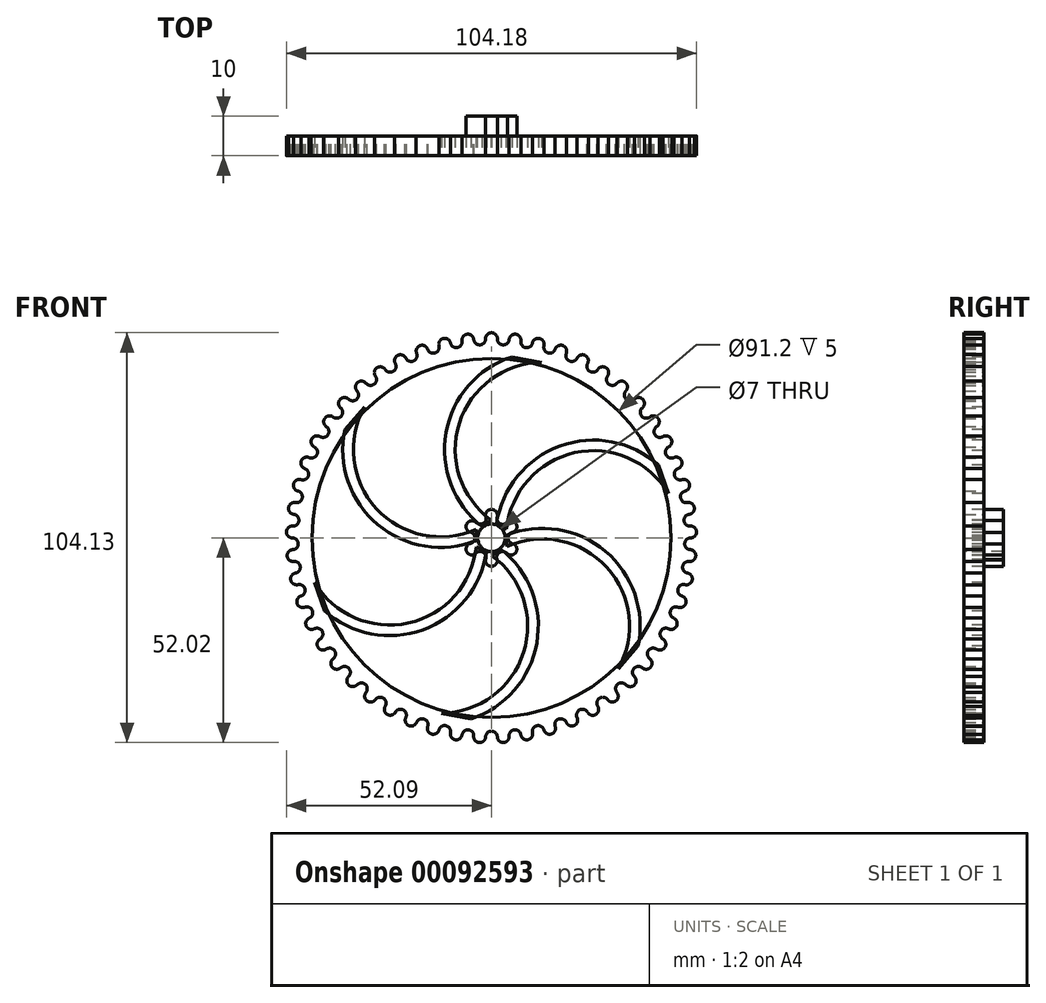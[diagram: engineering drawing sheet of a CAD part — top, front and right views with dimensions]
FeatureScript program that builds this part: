
annotation { "Feature Type Name" : "Feature", "Feature Type Description" : "" }
export const myFeature = defineFeature(function(context is Context, id is Id, definition is map)
    precondition{}
    {
        {
            var Q0;
            Q0=qCreatedBy(makeId("Front.planeOp"),FACE);
            var sketch = newSketch(context, id + "F0", { "sketchPlane" : qUnion([Q0])});
            skLineSegment(sketch, "E0", {"start": v(0, 0) * mm, "end": v(0, 50.61) * mm});
            skArc(sketch, "E1", {"start": v(1.5, 50.57) * mm, "mid": v(0.01, 52.11) * mm, "end": v(-1.5, 50.59) * mm});
            skArc(sketch, "E2", {"start": v(1.5, 50.57) * mm, "mid": v(2.92, 49.02) * mm, "end": v(4.5, 50.41) * mm});
            skLineSegment(sketch, "E3", {"start": v(4.5, 50.41) * mm, "end": v(4.47, 50.43) * mm});
            skArc(sketch, "E4.1.0", {"start": v(-4.5, 50.39) * mm, "mid": v(-6.15, 51.75) * mm, "end": v(-7.47, 50.06) * mm});
            skArc(sketch, "E4.1.1", {"start": v(-4.5, 50.39) * mm, "mid": v(-2.9, 49.03) * mm, "end": v(-1.5, 50.59) * mm});
            skLineSegment(sketch, "E4.1.2", {"start": v(-1.5, 50.59) * mm, "end": v(-1.52, 50.6) * mm});
            skArc(sketch, "E4.2.0", {"start": v(-10.42, 49.5) * mm, "mid": v(-12.23, 50.66) * mm, "end": v(-13.34, 48.82) * mm});
            skArc(sketch, "E4.2.1", {"start": v(-10.42, 49.5) * mm, "mid": v(-8.68, 48.34) * mm, "end": v(-7.47, 50.06) * mm});
            skLineSegment(sketch, "E4.2.2", {"start": v(-7.47, 50.06) * mm, "end": v(-7.5, 50.07) * mm});
            skArc(sketch, "E4.3.0", {"start": v(-16.2, 47.92) * mm, "mid": v(-18.13, 48.85) * mm, "end": v(-19.02, 46.9) * mm});
            skArc(sketch, "E4.3.1", {"start": v(-16.2, 47.92) * mm, "mid": v(-14.33, 46.97) * mm, "end": v(-13.34, 48.82) * mm});
            skLineSegment(sketch, "E4.3.2", {"start": v(-13.34, 48.82) * mm, "end": v(-13.37, 48.84) * mm});
            skArc(sketch, "E4.4.0", {"start": v(-21.76, 45.67) * mm, "mid": v(-23.79, 46.37) * mm, "end": v(-24.43, 44.32) * mm});
            skArc(sketch, "E4.4.1", {"start": v(-21.76, 45.67) * mm, "mid": v(-19.79, 44.95) * mm, "end": v(-19.02, 46.9) * mm});
            skLineSegment(sketch, "E4.4.2", {"start": v(-19.02, 46.9) * mm, "end": v(-19.05, 46.91) * mm});
            skArc(sketch, "E4.5.0", {"start": v(-27, 42.78) * mm, "mid": v(-29.1, 43.23) * mm, "end": v(-29.5, 41.12) * mm});
            skArc(sketch, "E4.5.1", {"start": v(-27, 42.78) * mm, "mid": v(-24.96, 42.3) * mm, "end": v(-24.43, 44.32) * mm});
            skLineSegment(sketch, "E4.5.2", {"start": v(-24.43, 44.32) * mm, "end": v(-24.46, 44.33) * mm});
            skArc(sketch, "E4.6.0", {"start": v(-31.88, 39.28) * mm, "mid": v(-34.01, 39.48) * mm, "end": v(-34.16, 37.34) * mm});
            skArc(sketch, "E4.6.1", {"start": v(-31.88, 39.28) * mm, "mid": v(-29.8, 39.04) * mm, "end": v(-29.5, 41.12) * mm});
            skLineSegment(sketch, "E4.6.2", {"start": v(-29.5, 41.12) * mm, "end": v(-29.54, 41.13) * mm});
            skArc(sketch, "E4.7.0", {"start": v(-36.3, 35.24) * mm, "mid": v(-38.44, 35.18) * mm, "end": v(-38.34, 33.04) * mm});
            skArc(sketch, "E4.7.1", {"start": v(-36.3, 35.24) * mm, "mid": v(-34.2, 35.25) * mm, "end": v(-34.16, 37.34) * mm});
            skLineSegment(sketch, "E4.7.2", {"start": v(-34.16, 37.34) * mm, "end": v(-34.2, 37.34) * mm});
            skArc(sketch, "E4.8.0", {"start": v(-40.21, 30.7) * mm, "mid": v(-42.33, 30.39) * mm, "end": v(-41.98, 28.27) * mm});
            skArc(sketch, "E4.8.1", {"start": v(-40.21, 30.7) * mm, "mid": v(-38.13, 30.95) * mm, "end": v(-38.34, 33.04) * mm});
            skLineSegment(sketch, "E4.8.2", {"start": v(-38.34, 33.04) * mm, "end": v(-38.37, 33.04) * mm});
            skArc(sketch, "E4.9.0", {"start": v(-43.56, 25.73) * mm, "mid": v(-45.63, 25.17) * mm, "end": v(-45.03, 23.11) * mm});
            skArc(sketch, "E4.9.1", {"start": v(-43.56, 25.73) * mm, "mid": v(-41.52, 26.23) * mm, "end": v(-41.98, 28.27) * mm});
            skLineSegment(sketch, "E4.9.2", {"start": v(-41.98, 28.27) * mm, "end": v(-42, 28.27) * mm});
            skArc(sketch, "E4.10.0", {"start": v(-46.3, 20.4) * mm, "mid": v(-48.29, 19.6) * mm, "end": v(-47.44, 17.62) * mm});
            skArc(sketch, "E4.10.1", {"start": v(-46.3, 20.4) * mm, "mid": v(-44.33, 21.13) * mm, "end": v(-45.03, 23.11) * mm});
            skLineSegment(sketch, "E4.10.2", {"start": v(-45.03, 23.11) * mm, "end": v(-45.06, 23.1) * mm});
            skArc(sketch, "E4.11.0", {"start": v(-48.38, 14.78) * mm, "mid": v(-50.27, 13.75) * mm, "end": v(-49.2, 11.89) * mm});
            skArc(sketch, "E4.11.1", {"start": v(-48.38, 14.78) * mm, "mid": v(-46.52, 15.74) * mm, "end": v(-47.44, 17.62) * mm});
            skLineSegment(sketch, "E4.11.2", {"start": v(-47.44, 17.62) * mm, "end": v(-47.47, 17.6) * mm});
            skArc(sketch, "E4.12.0", {"start": v(-49.8, 8.95) * mm, "mid": v(-51.54, 7.7) * mm, "end": v(-50.26, 5.99) * mm});
            skArc(sketch, "E4.12.1", {"start": v(-49.8, 8.95) * mm, "mid": v(-48.06, 10.13) * mm, "end": v(-49.2, 11.89) * mm});
            skLineSegment(sketch, "E4.12.2", {"start": v(-49.2, 11.89) * mm, "end": v(-49.22, 11.87) * mm});
            skArc(sketch, "E4.13.0", {"start": v(-50.5, 3) * mm, "mid": v(-52.09, 1.56) * mm, "end": v(-50.61, 0) * mm});
            skArc(sketch, "E4.13.1", {"start": v(-50.5, 3) * mm, "mid": v(-48.92, 4.37) * mm, "end": v(-50.26, 5.99) * mm});
            skLineSegment(sketch, "E4.13.2", {"start": v(-50.26, 5.99) * mm, "end": v(-50.28, 5.97) * mm});
            skArc(sketch, "E4.14.0", {"start": v(-50.5, -3) * mm, "mid": v(-51.9, -4.62) * mm, "end": v(-50.26, -5.99) * mm});
            skArc(sketch, "E4.14.1", {"start": v(-50.5, -3) * mm, "mid": v(-49.1, -1.44) * mm, "end": v(-50.61, 0) * mm});
            skLineSegment(sketch, "E4.14.2", {"start": v(-50.61, 0) * mm, "end": v(-50.63, -0.02) * mm});
            skArc(sketch, "E4.15.0", {"start": v(-49.8, -8.95) * mm, "mid": v(-51, -10.72) * mm, "end": v(-49.2, -11.89) * mm});
            skArc(sketch, "E4.15.1", {"start": v(-49.8, -8.95) * mm, "mid": v(-48.57, -7.24) * mm, "end": v(-50.26, -5.99) * mm});
            skLineSegment(sketch, "E4.15.2", {"start": v(-50.26, -5.99) * mm, "end": v(-50.27, -6.01) * mm});
            skArc(sketch, "E4.16.0", {"start": v(-48.38, -14.77) * mm, "mid": v(-49.37, -16.68) * mm, "end": v(-47.44, -17.62) * mm});
            skArc(sketch, "E4.16.1", {"start": v(-48.38, -14.77) * mm, "mid": v(-47.38, -12.93) * mm, "end": v(-49.2, -11.89) * mm});
            skLineSegment(sketch, "E4.16.2", {"start": v(-49.2, -11.89) * mm, "end": v(-49.21, -11.91) * mm});
            skArc(sketch, "E4.17.0", {"start": v(-46.3, -20.4) * mm, "mid": v(-47.05, -22.4) * mm, "end": v(-45.03, -23.11) * mm});
            skArc(sketch, "E4.17.1", {"start": v(-46.3, -20.4) * mm, "mid": v(-45.52, -18.45) * mm, "end": v(-47.44, -17.62) * mm});
            skLineSegment(sketch, "E4.17.2", {"start": v(-47.44, -17.62) * mm, "end": v(-47.46, -17.65) * mm});
            skArc(sketch, "E4.18.0", {"start": v(-43.56, -25.73) * mm, "mid": v(-44.07, -27.8) * mm, "end": v(-41.98, -28.27) * mm});
            skArc(sketch, "E4.18.1", {"start": v(-43.56, -25.73) * mm, "mid": v(-43.01, -23.7) * mm, "end": v(-45.03, -23.11) * mm});
            skLineSegment(sketch, "E4.18.2", {"start": v(-45.03, -23.11) * mm, "end": v(-45.04, -23.14) * mm});
            skArc(sketch, "E4.19.0", {"start": v(-40.21, -30.7) * mm, "mid": v(-40.47, -32.83) * mm, "end": v(-38.34, -33.04) * mm});
            skArc(sketch, "E4.19.1", {"start": v(-40.21, -30.7) * mm, "mid": v(-39.9, -28.62) * mm, "end": v(-41.98, -28.27) * mm});
            skLineSegment(sketch, "E4.19.2", {"start": v(-41.98, -28.27) * mm, "end": v(-41.98, -28.3) * mm});
            skArc(sketch, "E4.20.0", {"start": v(-36.3, -35.24) * mm, "mid": v(-36.3, -37.38) * mm, "end": v(-34.16, -37.34) * mm});
            skArc(sketch, "E4.20.1", {"start": v(-36.3, -35.24) * mm, "mid": v(-36.24, -33.14) * mm, "end": v(-38.34, -33.04) * mm});
            skLineSegment(sketch, "E4.20.2", {"start": v(-38.34, -33.04) * mm, "end": v(-38.34, -33.07) * mm});
            skArc(sketch, "E4.21.0", {"start": v(-31.88, -39.28) * mm, "mid": v(-31.63, -41.41) * mm, "end": v(-29.5, -41.12) * mm});
            skArc(sketch, "E4.21.1", {"start": v(-31.88, -39.28) * mm, "mid": v(-32.07, -37.2) * mm, "end": v(-34.16, -37.34) * mm});
            skLineSegment(sketch, "E4.21.2", {"start": v(-34.16, -37.34) * mm, "end": v(-34.16, -37.37) * mm});
            skArc(sketch, "E4.22.0", {"start": v(-27, -42.78) * mm, "mid": v(-26.5, -44.86) * mm, "end": v(-24.43, -44.32) * mm});
            skArc(sketch, "E4.22.1", {"start": v(-27, -42.78) * mm, "mid": v(-27.45, -40.73) * mm, "end": v(-29.5, -41.12) * mm});
            skLineSegment(sketch, "E4.22.2", {"start": v(-29.5, -41.12) * mm, "end": v(-29.5, -41.15) * mm});
            skArc(sketch, "E4.23.0", {"start": v(-21.76, -45.67) * mm, "mid": v(-21.02, -47.69) * mm, "end": v(-19.02, -46.9) * mm});
            skArc(sketch, "E4.23.1", {"start": v(-21.76, -45.67) * mm, "mid": v(-22.44, -43.69) * mm, "end": v(-24.44, -44.32) * mm});
            skLineSegment(sketch, "E4.23.2", {"start": v(-24.44, -44.32) * mm, "end": v(-24.43, -44.35) * mm});
            skArc(sketch, "E4.24.0", {"start": v(-16.2, -47.92) * mm, "mid": v(-15.23, -49.84) * mm, "end": v(-13.34, -48.82) * mm});
            skArc(sketch, "E4.24.1", {"start": v(-16.2, -47.92) * mm, "mid": v(-17.11, -46.03) * mm, "end": v(-19.02, -46.9) * mm});
            skLineSegment(sketch, "E4.24.2", {"start": v(-19.02, -46.9) * mm, "end": v(-19, -46.93) * mm});
            skArc(sketch, "E4.25.0", {"start": v(-10.42, -49.5) * mm, "mid": v(-9.23, -51.29) * mm, "end": v(-7.47, -50.06) * mm});
            skArc(sketch, "E4.25.1", {"start": v(-10.42, -49.5) * mm, "mid": v(-11.55, -47.73) * mm, "end": v(-13.34, -48.82) * mm});
            skLineSegment(sketch, "E4.25.2", {"start": v(-13.34, -48.82) * mm, "end": v(-13.32, -48.85) * mm});
            skArc(sketch, "E4.26.0", {"start": v(-4.5, -50.39) * mm, "mid": v(-3.1, -52.02) * mm, "end": v(-1.5, -50.59) * mm});
            skArc(sketch, "E4.26.1", {"start": v(-4.5, -50.39) * mm, "mid": v(-5.82, -48.77) * mm, "end": v(-7.47, -50.06) * mm});
            skLineSegment(sketch, "E4.26.2", {"start": v(-7.47, -50.06) * mm, "end": v(-7.45, -50.08) * mm});
            skArc(sketch, "E4.27.0", {"start": v(1.5, -50.57) * mm, "mid": v(3.08, -52.02) * mm, "end": v(4.5, -50.41) * mm});
            skArc(sketch, "E4.27.1", {"start": v(1.5, -50.57) * mm, "mid": v(-0.01, -49.11) * mm, "end": v(-1.5, -50.59) * mm});
            skLineSegment(sketch, "E4.27.2", {"start": v(-1.5, -50.59) * mm, "end": v(-1.48, -50.61) * mm});
            skArc(sketch, "E4.28.0", {"start": v(7.47, -50.03) * mm, "mid": v(9.2, -51.3) * mm, "end": v(10.42, -49.53) * mm});
            skArc(sketch, "E4.28.1", {"start": v(7.47, -50.03) * mm, "mid": v(5.8, -48.77) * mm, "end": v(4.5, -50.41) * mm});
            skLineSegment(sketch, "E4.28.2", {"start": v(4.5, -50.41) * mm, "end": v(4.52, -50.43) * mm});
            skArc(sketch, "E4.29.0", {"start": v(13.33, -48.8) * mm, "mid": v(15.2, -49.84) * mm, "end": v(16.2, -47.95) * mm});
            skArc(sketch, "E4.29.1", {"start": v(13.33, -48.8) * mm, "mid": v(11.52, -47.74) * mm, "end": v(10.42, -49.53) * mm});
            skLineSegment(sketch, "E4.29.2", {"start": v(10.42, -49.53) * mm, "end": v(10.45, -49.54) * mm});
            skArc(sketch, "E4.30.0", {"start": v(19.01, -46.88) * mm, "mid": v(21, -47.7) * mm, "end": v(21.77, -45.7) * mm});
            skArc(sketch, "E4.30.1", {"start": v(19.01, -46.88) * mm, "mid": v(17.09, -46.04) * mm, "end": v(16.2, -47.95) * mm});
            skLineSegment(sketch, "E4.30.2", {"start": v(16.2, -47.95) * mm, "end": v(16.24, -47.96) * mm});
            skArc(sketch, "E4.31.0", {"start": v(24.42, -44.3) * mm, "mid": v(26.5, -44.88) * mm, "end": v(27.02, -42.8) * mm});
            skArc(sketch, "E4.31.1", {"start": v(24.42, -44.3) * mm, "mid": v(22.42, -43.7) * mm, "end": v(21.77, -45.7) * mm});
            skLineSegment(sketch, "E4.31.2", {"start": v(21.77, -45.7) * mm, "end": v(21.8, -45.7) * mm});
            skArc(sketch, "E4.32.0", {"start": v(29.5, -41.1) * mm, "mid": v(31.61, -41.43) * mm, "end": v(31.89, -39.3) * mm});
            skArc(sketch, "E4.32.1", {"start": v(29.5, -41.1) * mm, "mid": v(27.43, -40.74) * mm, "end": v(27.02, -42.8) * mm});
            skLineSegment(sketch, "E4.32.2", {"start": v(27.02, -42.8) * mm, "end": v(27.05, -42.8) * mm});
            skArc(sketch, "E4.33.0", {"start": v(34.15, -37.33) * mm, "mid": v(36.3, -37.4) * mm, "end": v(36.31, -35.25) * mm});
            skArc(sketch, "E4.33.1", {"start": v(34.15, -37.33) * mm, "mid": v(32.05, -37.21) * mm, "end": v(31.89, -39.3) * mm});
            skLineSegment(sketch, "E4.33.2", {"start": v(31.89, -39.3) * mm, "end": v(31.92, -39.3) * mm});
            skArc(sketch, "E4.34.0", {"start": v(38.32, -33.03) * mm, "mid": v(40.46, -32.84) * mm, "end": v(40.23, -30.71) * mm});
            skArc(sketch, "E4.34.1", {"start": v(38.32, -33.03) * mm, "mid": v(36.23, -33.16) * mm, "end": v(36.31, -35.25) * mm});
            skLineSegment(sketch, "E4.34.2", {"start": v(36.31, -35.25) * mm, "end": v(36.34, -35.25) * mm});
            skArc(sketch, "E4.35.0", {"start": v(41.96, -28.26) * mm, "mid": v(44.06, -27.83) * mm, "end": v(43.58, -25.74) * mm});
            skArc(sketch, "E4.35.1", {"start": v(41.96, -28.26) * mm, "mid": v(39.9, -28.64) * mm, "end": v(40.23, -30.71) * mm});
            skLineSegment(sketch, "E4.35.2", {"start": v(40.23, -30.71) * mm, "end": v(40.26, -30.7) * mm});
            skArc(sketch, "E4.36.0", {"start": v(45, -23.1) * mm, "mid": v(47.04, -22.42) * mm, "end": v(46.32, -20.4) * mm});
            skArc(sketch, "E4.36.1", {"start": v(45, -23.1) * mm, "mid": v(43, -23.72) * mm, "end": v(43.58, -25.74) * mm});
            skLineSegment(sketch, "E4.36.2", {"start": v(43.58, -25.74) * mm, "end": v(43.6, -25.73) * mm});
            skArc(sketch, "E4.37.0", {"start": v(47.42, -17.62) * mm, "mid": v(49.36, -16.7) * mm, "end": v(48.4, -14.78) * mm});
            skArc(sketch, "E4.37.1", {"start": v(47.42, -17.62) * mm, "mid": v(45.5, -18.47) * mm, "end": v(46.32, -20.4) * mm});
            skLineSegment(sketch, "E4.37.2", {"start": v(46.32, -20.4) * mm, "end": v(46.35, -20.4) * mm});
            skArc(sketch, "E4.38.0", {"start": v(49.17, -11.88) * mm, "mid": v(51, -10.74) * mm, "end": v(49.81, -8.95) * mm});
            skArc(sketch, "E4.38.1", {"start": v(49.17, -11.88) * mm, "mid": v(47.37, -12.96) * mm, "end": v(48.4, -14.78) * mm});
            skLineSegment(sketch, "E4.38.2", {"start": v(48.4, -14.78) * mm, "end": v(48.43, -14.77) * mm});
            skArc(sketch, "E4.39.0", {"start": v(50.23, -5.98) * mm, "mid": v(51.9, -4.64) * mm, "end": v(50.52, -3) * mm});
            skArc(sketch, "E4.39.1", {"start": v(50.23, -5.98) * mm, "mid": v(48.57, -7.26) * mm, "end": v(49.81, -8.95) * mm});
            skLineSegment(sketch, "E4.39.2", {"start": v(49.81, -8.95) * mm, "end": v(49.84, -8.93) * mm});
            skArc(sketch, "E4.40.0", {"start": v(50.59, 0) * mm, "mid": v(52.09, 1.53) * mm, "end": v(50.52, 3) * mm});
            skArc(sketch, "E4.40.1", {"start": v(50.59, 0) * mm, "mid": v(49.09, -1.47) * mm, "end": v(50.52, -3) * mm});
            skLineSegment(sketch, "E4.40.2", {"start": v(50.52, -3) * mm, "end": v(50.55, -2.98) * mm});
            skArc(sketch, "E4.41.0", {"start": v(50.23, 5.98) * mm, "mid": v(51.54, 7.68) * mm, "end": v(49.81, 8.95) * mm});
            skArc(sketch, "E4.41.1", {"start": v(50.23, 5.98) * mm, "mid": v(48.92, 4.35) * mm, "end": v(50.52, 3) * mm});
            skLineSegment(sketch, "E4.41.2", {"start": v(50.52, 3) * mm, "end": v(50.54, 3.02) * mm});
            skArc(sketch, "E4.42.0", {"start": v(49.17, 11.88) * mm, "mid": v(50.27, 13.73) * mm, "end": v(48.4, 14.78) * mm});
            skArc(sketch, "E4.42.1", {"start": v(49.17, 11.88) * mm, "mid": v(48.06, 10.1) * mm, "end": v(49.81, 8.95) * mm});
            skLineSegment(sketch, "E4.42.2", {"start": v(49.81, 8.95) * mm, "end": v(49.83, 8.98) * mm});
            skArc(sketch, "E4.43.0", {"start": v(47.42, 17.62) * mm, "mid": v(48.3, 19.57) * mm, "end": v(46.32, 20.4) * mm});
            skArc(sketch, "E4.43.1", {"start": v(47.42, 17.62) * mm, "mid": v(46.53, 15.72) * mm, "end": v(48.4, 14.78) * mm});
            skLineSegment(sketch, "E4.43.2", {"start": v(48.4, 14.78) * mm, "end": v(48.42, 14.8) * mm});
            skArc(sketch, "E4.44.0", {"start": v(45, 23.1) * mm, "mid": v(45.64, 25.15) * mm, "end": v(43.58, 25.74) * mm});
            skArc(sketch, "E4.44.1", {"start": v(45, 23.1) * mm, "mid": v(44.34, 21.11) * mm, "end": v(46.32, 20.4) * mm});
            skLineSegment(sketch, "E4.44.2", {"start": v(46.32, 20.4) * mm, "end": v(46.33, 20.43) * mm});
            skArc(sketch, "E4.45.0", {"start": v(41.96, 28.26) * mm, "mid": v(42.35, 30.37) * mm, "end": v(40.23, 30.71) * mm});
            skArc(sketch, "E4.45.1", {"start": v(41.96, 28.26) * mm, "mid": v(41.53, 26.2) * mm, "end": v(43.58, 25.74) * mm});
            skLineSegment(sketch, "E4.45.2", {"start": v(43.58, 25.74) * mm, "end": v(43.59, 25.77) * mm});
            skArc(sketch, "E4.46.0", {"start": v(38.32, 33.03) * mm, "mid": v(38.46, 35.17) * mm, "end": v(36.31, 35.25) * mm});
            skArc(sketch, "E4.46.1", {"start": v(38.32, 33.03) * mm, "mid": v(38.14, 30.94) * mm, "end": v(40.23, 30.71) * mm});
            skLineSegment(sketch, "E4.46.2", {"start": v(40.23, 30.71) * mm, "end": v(40.23, 30.74) * mm});
            skArc(sketch, "E4.47.0", {"start": v(34.15, 37.33) * mm, "mid": v(34.03, 39.47) * mm, "end": v(31.89, 39.3) * mm});
            skArc(sketch, "E4.47.1", {"start": v(34.15, 37.33) * mm, "mid": v(34.22, 35.23) * mm, "end": v(36.31, 35.25) * mm});
            skLineSegment(sketch, "E4.47.2", {"start": v(36.31, 35.25) * mm, "end": v(36.31, 35.28) * mm});
            skArc(sketch, "E4.48.0", {"start": v(29.5, 41.1) * mm, "mid": v(29.12, 43.22) * mm, "end": v(27.02, 42.8) * mm});
            skArc(sketch, "E4.48.1", {"start": v(29.5, 41.1) * mm, "mid": v(29.81, 39.03) * mm, "end": v(31.9, 39.3) * mm});
            skLineSegment(sketch, "E4.48.2", {"start": v(31.9, 39.3) * mm, "end": v(31.89, 39.33) * mm});
            skArc(sketch, "E4.49.0", {"start": v(24.42, 44.3) * mm, "mid": v(23.8, 46.36) * mm, "end": v(21.77, 45.7) * mm});
            skArc(sketch, "E4.49.1", {"start": v(24.42, 44.3) * mm, "mid": v(24.98, 42.28) * mm, "end": v(27.02, 42.8) * mm});
            skLineSegment(sketch, "E4.49.2", {"start": v(27.02, 42.8) * mm, "end": v(27.01, 42.83) * mm});
            skArc(sketch, "E4.50.0", {"start": v(19.01, 46.88) * mm, "mid": v(18.16, 48.85) * mm, "end": v(16.2, 47.95) * mm});
            skArc(sketch, "E4.50.1", {"start": v(19.01, 46.88) * mm, "mid": v(19.8, 44.94) * mm, "end": v(21.77, 45.7) * mm});
            skLineSegment(sketch, "E4.50.2", {"start": v(21.77, 45.7) * mm, "end": v(21.76, 45.72) * mm});
            skArc(sketch, "E4.51.0", {"start": v(13.33, 48.8) * mm, "mid": v(12.25, 50.65) * mm, "end": v(10.42, 49.53) * mm});
            skArc(sketch, "E4.51.1", {"start": v(13.33, 48.8) * mm, "mid": v(14.35, 46.97) * mm, "end": v(16.2, 47.95) * mm});
            skLineSegment(sketch, "E4.51.2", {"start": v(16.2, 47.95) * mm, "end": v(16.2, 47.97) * mm});
            skArc(sketch, "E4.52.0", {"start": v(7.47, 50.03) * mm, "mid": v(6.17, 51.74) * mm, "end": v(4.5, 50.41) * mm});
            skArc(sketch, "E4.52.1", {"start": v(7.47, 50.03) * mm, "mid": v(8.7, 48.34) * mm, "end": v(10.43, 49.53) * mm});
            skLineSegment(sketch, "E4.52.2", {"start": v(10.43, 49.53) * mm, "end": v(10.4, 49.55) * mm});
            skPoint(sketch, "E4.center", {"position": v(0, 0) * mm});
            skSolve(sketch);
        }
        {
            var Q0;
            {var subQ135=sQuery(id+"F0.wireOp",EDGE,"E2");Q0=makeQuery(id+"F0.imprint","IMPRINT",FACE,{"disambiguationData":[TD([[makeQuery(id+"F0.imprint","IMPRINT",EDGE,{"derivedFrom":subQ135}),-1.0]])]});}
            extrude(context, id + "F1", {"entities" : qUnion([Q0]), "depth" : 5 * mm});
        }
        {
            var Q0;
            Q0=makeQuery(id+"F1.opExtrude","CAP_FACE",FACE,{"disambiguationData":[OSD([sQuery(id+"F0.wireOp",EDGE,"E1"),sQuery(id+"F0.wireOp",EDGE,"E2"),sQuery(id+"F0.wireOp",EDGE,"E3"),sQuery(id+"F0.wireOp",EDGE,"E4.1.0"),sQuery(id+"F0.wireOp",EDGE,"E4.1.1"),sQuery(id+"F0.wireOp",EDGE,"E4.1.2"),sQuery(id+"F0.wireOp",EDGE,"E4.2.0"),sQuery(id+"F0.wireOp",EDGE,"E4.2.1"),sQuery(id+"F0.wireOp",EDGE,"E4.2.2"),sQuery(id+"F0.wireOp",EDGE,"E4.3.0"),sQuery(id+"F0.wireOp",EDGE,"E4.3.1"),sQuery(id+"F0.wireOp",EDGE,"E4.3.2"),sQuery(id+"F0.wireOp",EDGE,"E4.4.0"),sQuery(id+"F0.wireOp",EDGE,"E4.4.1"),sQuery(id+"F0.wireOp",EDGE,"E4.4.2"),sQuery(id+"F0.wireOp",EDGE,"E4.5.0"),sQuery(id+"F0.wireOp",EDGE,"E4.5.1"),sQuery(id+"F0.wireOp",EDGE,"E4.5.2"),sQuery(id+"F0.wireOp",EDGE,"E4.6.0"),sQuery(id+"F0.wireOp",EDGE,"E4.6.1"),sQuery(id+"F0.wireOp",EDGE,"E4.6.2"),sQuery(id+"F0.wireOp",EDGE,"E4.7.0"),sQuery(id+"F0.wireOp",EDGE,"E4.7.1"),sQuery(id+"F0.wireOp",EDGE,"E4.7.2"),sQuery(id+"F0.wireOp",EDGE,"E4.8.0"),sQuery(id+"F0.wireOp",EDGE,"E4.8.1"),sQuery(id+"F0.wireOp",EDGE,"E4.8.2"),sQuery(id+"F0.wireOp",EDGE,"E4.9.0"),sQuery(id+"F0.wireOp",EDGE,"E4.9.1"),sQuery(id+"F0.wireOp",EDGE,"E4.9.2"),sQuery(id+"F0.wireOp",EDGE,"E4.10.0"),sQuery(id+"F0.wireOp",EDGE,"E4.10.1"),sQuery(id+"F0.wireOp",EDGE,"E4.10.2"),sQuery(id+"F0.wireOp",EDGE,"E4.11.0"),sQuery(id+"F0.wireOp",EDGE,"E4.11.1"),sQuery(id+"F0.wireOp",EDGE,"E4.11.2"),sQuery(id+"F0.wireOp",EDGE,"E4.12.0"),sQuery(id+"F0.wireOp",EDGE,"E4.12.1"),sQuery(id+"F0.wireOp",EDGE,"E4.12.2"),sQuery(id+"F0.wireOp",EDGE,"E4.13.0"),sQuery(id+"F0.wireOp",EDGE,"E4.13.1"),sQuery(id+"F0.wireOp",EDGE,"E4.13.2"),sQuery(id+"F0.wireOp",EDGE,"E4.14.0"),sQuery(id+"F0.wireOp",EDGE,"E4.14.1"),sQuery(id+"F0.wireOp",EDGE,"E4.14.2"),sQuery(id+"F0.wireOp",EDGE,"E4.15.0"),sQuery(id+"F0.wireOp",EDGE,"E4.15.1"),sQuery(id+"F0.wireOp",EDGE,"E4.15.2"),sQuery(id+"F0.wireOp",EDGE,"E4.16.0"),sQuery(id+"F0.wireOp",EDGE,"E4.16.1"),sQuery(id+"F0.wireOp",EDGE,"E4.16.2"),sQuery(id+"F0.wireOp",EDGE,"E4.17.0"),sQuery(id+"F0.wireOp",EDGE,"E4.17.1"),sQuery(id+"F0.wireOp",EDGE,"E4.17.2"),sQuery(id+"F0.wireOp",EDGE,"E4.18.0"),sQuery(id+"F0.wireOp",EDGE,"E4.18.1"),sQuery(id+"F0.wireOp",EDGE,"E4.18.2"),sQuery(id+"F0.wireOp",EDGE,"E4.19.0"),sQuery(id+"F0.wireOp",EDGE,"E4.19.1"),sQuery(id+"F0.wireOp",EDGE,"E4.19.2"),sQuery(id+"F0.wireOp",EDGE,"E4.20.0"),sQuery(id+"F0.wireOp",EDGE,"E4.20.1"),sQuery(id+"F0.wireOp",EDGE,"E4.20.2"),sQuery(id+"F0.wireOp",EDGE,"E4.21.0"),sQuery(id+"F0.wireOp",EDGE,"E4.21.1"),sQuery(id+"F0.wireOp",EDGE,"E4.21.2"),sQuery(id+"F0.wireOp",EDGE,"E4.22.0"),sQuery(id+"F0.wireOp",EDGE,"E4.22.1"),sQuery(id+"F0.wireOp",EDGE,"E4.22.2"),sQuery(id+"F0.wireOp",EDGE,"E4.23.0"),sQuery(id+"F0.wireOp",EDGE,"E4.23.1"),sQuery(id+"F0.wireOp",EDGE,"E4.23.2"),sQuery(id+"F0.wireOp",EDGE,"E4.24.0"),sQuery(id+"F0.wireOp",EDGE,"E4.24.1"),sQuery(id+"F0.wireOp",EDGE,"E4.24.2"),sQuery(id+"F0.wireOp",EDGE,"E4.25.0"),sQuery(id+"F0.wireOp",EDGE,"E4.25.1"),sQuery(id+"F0.wireOp",EDGE,"E4.25.2"),sQuery(id+"F0.wireOp",EDGE,"E4.26.0"),sQuery(id+"F0.wireOp",EDGE,"E4.26.1"),sQuery(id+"F0.wireOp",EDGE,"E4.26.2"),sQuery(id+"F0.wireOp",EDGE,"E4.27.0"),sQuery(id+"F0.wireOp",EDGE,"E4.27.1"),sQuery(id+"F0.wireOp",EDGE,"E4.27.2"),sQuery(id+"F0.wireOp",EDGE,"E4.28.0"),sQuery(id+"F0.wireOp",EDGE,"E4.28.1"),sQuery(id+"F0.wireOp",EDGE,"E4.28.2"),sQuery(id+"F0.wireOp",EDGE,"E4.29.0"),sQuery(id+"F0.wireOp",EDGE,"E4.29.1"),sQuery(id+"F0.wireOp",EDGE,"E4.29.2"),sQuery(id+"F0.wireOp",EDGE,"E4.30.0"),sQuery(id+"F0.wireOp",EDGE,"E4.30.1"),sQuery(id+"F0.wireOp",EDGE,"E4.30.2"),sQuery(id+"F0.wireOp",EDGE,"E4.31.0"),sQuery(id+"F0.wireOp",EDGE,"E4.31.1"),sQuery(id+"F0.wireOp",EDGE,"E4.31.2"),sQuery(id+"F0.wireOp",EDGE,"E4.32.0"),sQuery(id+"F0.wireOp",EDGE,"E4.32.1"),sQuery(id+"F0.wireOp",EDGE,"E4.32.2"),sQuery(id+"F0.wireOp",EDGE,"E4.33.0"),sQuery(id+"F0.wireOp",EDGE,"E4.33.1"),sQuery(id+"F0.wireOp",EDGE,"E4.33.2"),sQuery(id+"F0.wireOp",EDGE,"E4.34.0"),sQuery(id+"F0.wireOp",EDGE,"E4.34.1"),sQuery(id+"F0.wireOp",EDGE,"E4.34.2"),sQuery(id+"F0.wireOp",EDGE,"E4.35.0"),sQuery(id+"F0.wireOp",EDGE,"E4.35.1"),sQuery(id+"F0.wireOp",EDGE,"E4.35.2"),sQuery(id+"F0.wireOp",EDGE,"E4.36.0"),sQuery(id+"F0.wireOp",EDGE,"E4.36.1"),sQuery(id+"F0.wireOp",EDGE,"E4.36.2"),sQuery(id+"F0.wireOp",EDGE,"E4.37.0"),sQuery(id+"F0.wireOp",EDGE,"E4.37.1"),sQuery(id+"F0.wireOp",EDGE,"E4.37.2"),sQuery(id+"F0.wireOp",EDGE,"E4.38.0"),sQuery(id+"F0.wireOp",EDGE,"E4.38.1"),sQuery(id+"F0.wireOp",EDGE,"E4.38.2"),sQuery(id+"F0.wireOp",EDGE,"E4.39.0"),sQuery(id+"F0.wireOp",EDGE,"E4.39.1"),sQuery(id+"F0.wireOp",EDGE,"E4.39.2"),sQuery(id+"F0.wireOp",EDGE,"E4.40.0"),sQuery(id+"F0.wireOp",EDGE,"E4.40.1"),sQuery(id+"F0.wireOp",EDGE,"E4.40.2"),sQuery(id+"F0.wireOp",EDGE,"E4.41.0"),sQuery(id+"F0.wireOp",EDGE,"E4.41.1"),sQuery(id+"F0.wireOp",EDGE,"E4.41.2"),sQuery(id+"F0.wireOp",EDGE,"E4.42.0"),sQuery(id+"F0.wireOp",EDGE,"E4.42.1"),sQuery(id+"F0.wireOp",EDGE,"E4.42.2"),sQuery(id+"F0.wireOp",EDGE,"E4.43.0"),sQuery(id+"F0.wireOp",EDGE,"E4.43.1"),sQuery(id+"F0.wireOp",EDGE,"E4.43.2"),sQuery(id+"F0.wireOp",EDGE,"E4.44.0"),sQuery(id+"F0.wireOp",EDGE,"E4.44.1"),sQuery(id+"F0.wireOp",EDGE,"E4.44.2"),sQuery(id+"F0.wireOp",EDGE,"E4.45.0"),sQuery(id+"F0.wireOp",EDGE,"E4.45.1"),sQuery(id+"F0.wireOp",EDGE,"E4.45.2"),sQuery(id+"F0.wireOp",EDGE,"E4.46.0"),sQuery(id+"F0.wireOp",EDGE,"E4.46.1"),sQuery(id+"F0.wireOp",EDGE,"E4.46.2"),sQuery(id+"F0.wireOp",EDGE,"E4.47.0"),sQuery(id+"F0.wireOp",EDGE,"E4.47.1"),sQuery(id+"F0.wireOp",EDGE,"E4.47.2"),sQuery(id+"F0.wireOp",EDGE,"E4.48.0"),sQuery(id+"F0.wireOp",EDGE,"E4.48.1"),sQuery(id+"F0.wireOp",EDGE,"E4.48.2"),sQuery(id+"F0.wireOp",EDGE,"E4.49.0"),sQuery(id+"F0.wireOp",EDGE,"E4.49.1"),sQuery(id+"F0.wireOp",EDGE,"E4.49.2"),sQuery(id+"F0.wireOp",EDGE,"E4.50.0"),sQuery(id+"F0.wireOp",EDGE,"E4.50.1"),sQuery(id+"F0.wireOp",EDGE,"E4.50.2"),sQuery(id+"F0.wireOp",EDGE,"E4.51.0"),sQuery(id+"F0.wireOp",EDGE,"E4.51.1"),sQuery(id+"F0.wireOp",EDGE,"E4.51.2"),sQuery(id+"F0.wireOp",EDGE,"E4.52.0"),sQuery(id+"F0.wireOp",EDGE,"E4.52.1"),sQuery(id+"F0.wireOp",EDGE,"E4.52.2")])],"isStart":false});
            var sketch = newSketch(context, id + "F2", { "sketchPlane" : qUnion([Q0])});
            skSolve(sketch);
        }
        {
            var Q0;
            Q0=makeQuery(id+"F1.opExtrude","CAP_FACE",FACE,{"disambiguationData":[OSD([sQuery(id+"F0.wireOp",EDGE,"E1"),sQuery(id+"F0.wireOp",EDGE,"E2"),sQuery(id+"F0.wireOp",EDGE,"E3"),sQuery(id+"F0.wireOp",EDGE,"E4.1.0"),sQuery(id+"F0.wireOp",EDGE,"E4.1.1"),sQuery(id+"F0.wireOp",EDGE,"E4.1.2"),sQuery(id+"F0.wireOp",EDGE,"E4.2.0"),sQuery(id+"F0.wireOp",EDGE,"E4.2.1"),sQuery(id+"F0.wireOp",EDGE,"E4.2.2"),sQuery(id+"F0.wireOp",EDGE,"E4.3.0"),sQuery(id+"F0.wireOp",EDGE,"E4.3.1"),sQuery(id+"F0.wireOp",EDGE,"E4.3.2"),sQuery(id+"F0.wireOp",EDGE,"E4.4.0"),sQuery(id+"F0.wireOp",EDGE,"E4.4.1"),sQuery(id+"F0.wireOp",EDGE,"E4.4.2"),sQuery(id+"F0.wireOp",EDGE,"E4.5.0"),sQuery(id+"F0.wireOp",EDGE,"E4.5.1"),sQuery(id+"F0.wireOp",EDGE,"E4.5.2"),sQuery(id+"F0.wireOp",EDGE,"E4.6.0"),sQuery(id+"F0.wireOp",EDGE,"E4.6.1"),sQuery(id+"F0.wireOp",EDGE,"E4.6.2"),sQuery(id+"F0.wireOp",EDGE,"E4.7.0"),sQuery(id+"F0.wireOp",EDGE,"E4.7.1"),sQuery(id+"F0.wireOp",EDGE,"E4.7.2"),sQuery(id+"F0.wireOp",EDGE,"E4.8.0"),sQuery(id+"F0.wireOp",EDGE,"E4.8.1"),sQuery(id+"F0.wireOp",EDGE,"E4.8.2"),sQuery(id+"F0.wireOp",EDGE,"E4.9.0"),sQuery(id+"F0.wireOp",EDGE,"E4.9.1"),sQuery(id+"F0.wireOp",EDGE,"E4.9.2"),sQuery(id+"F0.wireOp",EDGE,"E4.10.0"),sQuery(id+"F0.wireOp",EDGE,"E4.10.1"),sQuery(id+"F0.wireOp",EDGE,"E4.10.2"),sQuery(id+"F0.wireOp",EDGE,"E4.11.0"),sQuery(id+"F0.wireOp",EDGE,"E4.11.1"),sQuery(id+"F0.wireOp",EDGE,"E4.11.2"),sQuery(id+"F0.wireOp",EDGE,"E4.12.0"),sQuery(id+"F0.wireOp",EDGE,"E4.12.1"),sQuery(id+"F0.wireOp",EDGE,"E4.12.2"),sQuery(id+"F0.wireOp",EDGE,"E4.13.0"),sQuery(id+"F0.wireOp",EDGE,"E4.13.1"),sQuery(id+"F0.wireOp",EDGE,"E4.13.2"),sQuery(id+"F0.wireOp",EDGE,"E4.14.0"),sQuery(id+"F0.wireOp",EDGE,"E4.14.1"),sQuery(id+"F0.wireOp",EDGE,"E4.14.2"),sQuery(id+"F0.wireOp",EDGE,"E4.15.0"),sQuery(id+"F0.wireOp",EDGE,"E4.15.1"),sQuery(id+"F0.wireOp",EDGE,"E4.15.2"),sQuery(id+"F0.wireOp",EDGE,"E4.16.0"),sQuery(id+"F0.wireOp",EDGE,"E4.16.1"),sQuery(id+"F0.wireOp",EDGE,"E4.16.2"),sQuery(id+"F0.wireOp",EDGE,"E4.17.0"),sQuery(id+"F0.wireOp",EDGE,"E4.17.1"),sQuery(id+"F0.wireOp",EDGE,"E4.17.2"),sQuery(id+"F0.wireOp",EDGE,"E4.18.0"),sQuery(id+"F0.wireOp",EDGE,"E4.18.1"),sQuery(id+"F0.wireOp",EDGE,"E4.18.2"),sQuery(id+"F0.wireOp",EDGE,"E4.19.0"),sQuery(id+"F0.wireOp",EDGE,"E4.19.1"),sQuery(id+"F0.wireOp",EDGE,"E4.19.2"),sQuery(id+"F0.wireOp",EDGE,"E4.20.0"),sQuery(id+"F0.wireOp",EDGE,"E4.20.1"),sQuery(id+"F0.wireOp",EDGE,"E4.20.2"),sQuery(id+"F0.wireOp",EDGE,"E4.21.0"),sQuery(id+"F0.wireOp",EDGE,"E4.21.1"),sQuery(id+"F0.wireOp",EDGE,"E4.21.2"),sQuery(id+"F0.wireOp",EDGE,"E4.22.0"),sQuery(id+"F0.wireOp",EDGE,"E4.22.1"),sQuery(id+"F0.wireOp",EDGE,"E4.22.2"),sQuery(id+"F0.wireOp",EDGE,"E4.23.0"),sQuery(id+"F0.wireOp",EDGE,"E4.23.1"),sQuery(id+"F0.wireOp",EDGE,"E4.23.2"),sQuery(id+"F0.wireOp",EDGE,"E4.24.0"),sQuery(id+"F0.wireOp",EDGE,"E4.24.1"),sQuery(id+"F0.wireOp",EDGE,"E4.24.2"),sQuery(id+"F0.wireOp",EDGE,"E4.25.0"),sQuery(id+"F0.wireOp",EDGE,"E4.25.1"),sQuery(id+"F0.wireOp",EDGE,"E4.25.2"),sQuery(id+"F0.wireOp",EDGE,"E4.26.0"),sQuery(id+"F0.wireOp",EDGE,"E4.26.1"),sQuery(id+"F0.wireOp",EDGE,"E4.26.2"),sQuery(id+"F0.wireOp",EDGE,"E4.27.0"),sQuery(id+"F0.wireOp",EDGE,"E4.27.1"),sQuery(id+"F0.wireOp",EDGE,"E4.27.2"),sQuery(id+"F0.wireOp",EDGE,"E4.28.0"),sQuery(id+"F0.wireOp",EDGE,"E4.28.1"),sQuery(id+"F0.wireOp",EDGE,"E4.28.2"),sQuery(id+"F0.wireOp",EDGE,"E4.29.0"),sQuery(id+"F0.wireOp",EDGE,"E4.29.1"),sQuery(id+"F0.wireOp",EDGE,"E4.29.2"),sQuery(id+"F0.wireOp",EDGE,"E4.30.0"),sQuery(id+"F0.wireOp",EDGE,"E4.30.1"),sQuery(id+"F0.wireOp",EDGE,"E4.30.2"),sQuery(id+"F0.wireOp",EDGE,"E4.31.0"),sQuery(id+"F0.wireOp",EDGE,"E4.31.1"),sQuery(id+"F0.wireOp",EDGE,"E4.31.2"),sQuery(id+"F0.wireOp",EDGE,"E4.32.0"),sQuery(id+"F0.wireOp",EDGE,"E4.32.1"),sQuery(id+"F0.wireOp",EDGE,"E4.32.2"),sQuery(id+"F0.wireOp",EDGE,"E4.33.0"),sQuery(id+"F0.wireOp",EDGE,"E4.33.1"),sQuery(id+"F0.wireOp",EDGE,"E4.33.2"),sQuery(id+"F0.wireOp",EDGE,"E4.34.0"),sQuery(id+"F0.wireOp",EDGE,"E4.34.1"),sQuery(id+"F0.wireOp",EDGE,"E4.34.2"),sQuery(id+"F0.wireOp",EDGE,"E4.35.0"),sQuery(id+"F0.wireOp",EDGE,"E4.35.1"),sQuery(id+"F0.wireOp",EDGE,"E4.35.2"),sQuery(id+"F0.wireOp",EDGE,"E4.36.0"),sQuery(id+"F0.wireOp",EDGE,"E4.36.1"),sQuery(id+"F0.wireOp",EDGE,"E4.36.2"),sQuery(id+"F0.wireOp",EDGE,"E4.37.0"),sQuery(id+"F0.wireOp",EDGE,"E4.37.1"),sQuery(id+"F0.wireOp",EDGE,"E4.37.2"),sQuery(id+"F0.wireOp",EDGE,"E4.38.0"),sQuery(id+"F0.wireOp",EDGE,"E4.38.1"),sQuery(id+"F0.wireOp",EDGE,"E4.38.2"),sQuery(id+"F0.wireOp",EDGE,"E4.39.0"),sQuery(id+"F0.wireOp",EDGE,"E4.39.1"),sQuery(id+"F0.wireOp",EDGE,"E4.39.2"),sQuery(id+"F0.wireOp",EDGE,"E4.40.0"),sQuery(id+"F0.wireOp",EDGE,"E4.40.1"),sQuery(id+"F0.wireOp",EDGE,"E4.40.2"),sQuery(id+"F0.wireOp",EDGE,"E4.41.0"),sQuery(id+"F0.wireOp",EDGE,"E4.41.1"),sQuery(id+"F0.wireOp",EDGE,"E4.41.2"),sQuery(id+"F0.wireOp",EDGE,"E4.42.0"),sQuery(id+"F0.wireOp",EDGE,"E4.42.1"),sQuery(id+"F0.wireOp",EDGE,"E4.42.2"),sQuery(id+"F0.wireOp",EDGE,"E4.43.0"),sQuery(id+"F0.wireOp",EDGE,"E4.43.1"),sQuery(id+"F0.wireOp",EDGE,"E4.43.2"),sQuery(id+"F0.wireOp",EDGE,"E4.44.0"),sQuery(id+"F0.wireOp",EDGE,"E4.44.1"),sQuery(id+"F0.wireOp",EDGE,"E4.44.2"),sQuery(id+"F0.wireOp",EDGE,"E4.45.0"),sQuery(id+"F0.wireOp",EDGE,"E4.45.1"),sQuery(id+"F0.wireOp",EDGE,"E4.45.2"),sQuery(id+"F0.wireOp",EDGE,"E4.46.0"),sQuery(id+"F0.wireOp",EDGE,"E4.46.1"),sQuery(id+"F0.wireOp",EDGE,"E4.46.2"),sQuery(id+"F0.wireOp",EDGE,"E4.47.0"),sQuery(id+"F0.wireOp",EDGE,"E4.47.1"),sQuery(id+"F0.wireOp",EDGE,"E4.47.2"),sQuery(id+"F0.wireOp",EDGE,"E4.48.0"),sQuery(id+"F0.wireOp",EDGE,"E4.48.1"),sQuery(id+"F0.wireOp",EDGE,"E4.48.2"),sQuery(id+"F0.wireOp",EDGE,"E4.49.0"),sQuery(id+"F0.wireOp",EDGE,"E4.49.1"),sQuery(id+"F0.wireOp",EDGE,"E4.49.2"),sQuery(id+"F0.wireOp",EDGE,"E4.50.0"),sQuery(id+"F0.wireOp",EDGE,"E4.50.1"),sQuery(id+"F0.wireOp",EDGE,"E4.50.2"),sQuery(id+"F0.wireOp",EDGE,"E4.51.0"),sQuery(id+"F0.wireOp",EDGE,"E4.51.1"),sQuery(id+"F0.wireOp",EDGE,"E4.51.2"),sQuery(id+"F0.wireOp",EDGE,"E4.52.0"),sQuery(id+"F0.wireOp",EDGE,"E4.52.1"),sQuery(id+"F0.wireOp",EDGE,"E4.52.2")])],"isStart":true});
            var sketch = newSketch(context, id + "F3", { "sketchPlane" : qUnion([Q0])});
            skPoint(sketch, "E5.endSnap0", {"position": v(49.1, -1.44) * mm});
            skLineSegment(sketch, "E6", {"start": v(49.1, 0) * mm, "end": v(45.6, 0) * mm});
            skCircle(sketch, "E7", {"center": v(0, 0) * mm, "radius": 45.6 * mm});
            skSolve(sketch);
        }
        {
            var Q0;
            Q0=makeQuery(id+"F3.imprint","IMPRINT",FACE,{"disambiguationData":[TD([[makeQuery(id+"F3.imprint","IMPRINT",EDGE,{"derivedFrom":sQuery(id+"F3.wireOp",EDGE,"E7")}),1.0]])]});
            extrude(context, id + "F4", {"entities" : qUnion([Q0]), "operationType" : NewBodyOperationType.REMOVE, "oppositeDirection" : true, "depth" : 10 * mm});
        }
        {
            var Q0;
            Q0=makeQuery(id+"F2.imprint","IMPRINT",FACE,{"disambiguationData":[TD([[makeQuery(id+"F2.imprint","IMPRINT",EDGE,{"derivedFrom":makeQuery(id+"F1.opExtrude","CAP_EDGE",EDGE,{"disambiguationData":[OSD([sQuery(id+"F0.wireOp",EDGE,"E1")])],"isStart":false})}),1.0]])]});
            var sketch = newSketch(context, id + "F5", { "sketchPlane" : qUnion([Q0])});
            skCircle(sketch, "E8", {"center": v(0, 0) * mm, "radius": 3.5 * mm});
            skArc(sketch, "E9", {"start": v(1.45, 5.34) * mm, "mid": v(0.1, 7.23) * mm, "end": v(-1.49, 5.53) * mm});
            skArc(sketch, "E10", {"start": v(1.45, 5.34) * mm, "mid": v(2.23, 3.6) * mm, "end": v(4.08, 4.02) * mm});
            skLineSegment(sketch, "E11", {"start": v(4.08, 4.02) * mm, "end": v(4.07, 4.11) * mm});
            skLineSegment(sketch, "E12", {"start": v(4.08, 4.02) * mm, "end": v(4.17, 4.01) * mm});
            skArc(sketch, "E13.1.0", {"start": v(-3.9, 3.92) * mm, "mid": v(-6.2, 3.7) * mm, "end": v(-5.54, 1.48) * mm});
            skArc(sketch, "E13.1.1", {"start": v(-3.9, 3.92) * mm, "mid": v(-2, 3.73) * mm, "end": v(-1.44, 5.54) * mm});
            skLineSegment(sketch, "E13.1.2", {"start": v(-1.44, 5.54) * mm, "end": v(-1.39, 5.62) * mm});
            skLineSegment(sketch, "E13.1.3", {"start": v(-1.44, 5.54) * mm, "end": v(-1.53, 5.58) * mm});
            skArc(sketch, "E13.2.0", {"start": v(-5.35, -1.41) * mm, "mid": v(-6.3, -3.53) * mm, "end": v(-4.05, -4.05) * mm});
            skArc(sketch, "E13.2.1", {"start": v(-5.35, -1.41) * mm, "mid": v(-4.23, 0.13) * mm, "end": v(-5.52, 1.52) * mm});
            skLineSegment(sketch, "E13.2.2", {"start": v(-5.52, 1.52) * mm, "end": v(-5.56, 1.6) * mm});
            skLineSegment(sketch, "E13.2.3", {"start": v(-5.52, 1.52) * mm, "end": v(-5.6, 1.46) * mm});
            skArc(sketch, "E13.3.0", {"start": v(-1.45, -5.34) * mm, "mid": v(-0.1, -7.23) * mm, "end": v(1.49, -5.53) * mm});
            skArc(sketch, "E13.3.1", {"start": v(-1.45, -5.34) * mm, "mid": v(-2.23, -3.6) * mm, "end": v(-4.08, -4.02) * mm});
            skLineSegment(sketch, "E13.3.2", {"start": v(-4.08, -4.02) * mm, "end": v(-4.17, -4.01) * mm});
            skLineSegment(sketch, "E13.3.3", {"start": v(-4.08, -4.02) * mm, "end": v(-4.07, -4.11) * mm});
            skArc(sketch, "E13.4.0", {"start": v(3.9, -3.92) * mm, "mid": v(6.2, -3.7) * mm, "end": v(5.54, -1.48) * mm});
            skArc(sketch, "E13.4.1", {"start": v(3.9, -3.92) * mm, "mid": v(2, -3.73) * mm, "end": v(1.44, -5.54) * mm});
            skLineSegment(sketch, "E13.4.2", {"start": v(1.44, -5.54) * mm, "end": v(1.39, -5.62) * mm});
            skLineSegment(sketch, "E13.4.3", {"start": v(1.44, -5.54) * mm, "end": v(1.53, -5.58) * mm});
            skArc(sketch, "E13.5.0", {"start": v(5.35, 1.41) * mm, "mid": v(6.3, 3.53) * mm, "end": v(4.05, 4.05) * mm});
            skArc(sketch, "E13.5.1", {"start": v(5.35, 1.41) * mm, "mid": v(4.23, -0.13) * mm, "end": v(5.52, -1.52) * mm});
            skLineSegment(sketch, "E13.5.2", {"start": v(5.52, -1.52) * mm, "end": v(5.56, -1.6) * mm});
            skLineSegment(sketch, "E13.5.3", {"start": v(5.52, -1.52) * mm, "end": v(5.6, -1.46) * mm});
            skSolve(sketch);
        }
        {
            var Q0;
            Q0 = qSketchRegion(id + "F5", true);
            extrude(context, id + "F6", {"entities" : qUnion([Q0]), "oppositeDirection" : true, "depth" : 10 * mm});
        }
        {
            var Q0;
            Q0=makeQuery(id+"F2.imprint","IMPRINT",FACE,{"disambiguationData":[TD([[makeQuery(id+"F2.imprint","IMPRINT",EDGE,{"derivedFrom":makeQuery(id+"F1.opExtrude","CAP_EDGE",EDGE,{"disambiguationData":[OSD([sQuery(id+"F0.wireOp",EDGE,"E1")])],"isStart":false})}),1.0]])]});
            var sketch = newSketch(context, id + "F7", { "sketchPlane" : qUnion([Q0])});
            skLineSegment(sketch, "E14", {"start": v(0, 0) * mm, "end": v(51.76, 0) * mm});
            skArc(sketch, "E15", {"start": v(42.43, 18.52) * mm, "mid": v(17.4, 23.35) * mm, "end": v(1.3, 3.56) * mm});
            skArc(sketch, "E16", {"start": v(44.92, 11.3) * mm, "mid": v(21.14, 21.63) * mm, "end": v(3.86, 2.3) * mm});
            skLineSegment(sketch, "E17", {"start": v(42.43, 18.52) * mm, "end": v(44.92, 11.3) * mm});
            skLineSegment(sketch, "E18", {"start": v(1.3, 3.56) * mm, "end": v(3.86, 2.3) * mm});
            skLineSegment(sketch, "E19.1.0", {"start": v(5.18, 46.01) * mm, "end": v(12.67, 44.56) * mm});
            skArc(sketch, "E19.1.1", {"start": v(5.18, 46.01) * mm, "mid": v(-11.52, 26.73) * mm, "end": v(-2.44, 2.9) * mm});
            skArc(sketch, "E19.1.2", {"start": v(12.67, 44.56) * mm, "mid": v(-8.16, 29.12) * mm, "end": v(-0.07, 4.5) * mm});
            skLineSegment(sketch, "E19.1.3", {"start": v(-2.44, 2.9) * mm, "end": v(-0.07, 4.5) * mm});
            skLineSegment(sketch, "E19.2.0", {"start": v(-37.26, 27.49) * mm, "end": v(-32.25, 33.25) * mm});
            skArc(sketch, "E19.2.1", {"start": v(-37.26, 27.49) * mm, "mid": v(-28.91, 3.39) * mm, "end": v(-3.73, -0.66) * mm});
            skArc(sketch, "E19.2.2", {"start": v(-32.25, 33.25) * mm, "mid": v(-29.3, 7.5) * mm, "end": v(-3.93, 2.19) * mm});
            skLineSegment(sketch, "E19.2.3", {"start": v(-3.73, -0.66) * mm, "end": v(-3.93, 2.19) * mm});
            skLineSegment(sketch, "E19.3.0", {"start": v(-42.43, -18.52) * mm, "end": v(-44.92, -11.3) * mm});
            skArc(sketch, "E19.3.1", {"start": v(-42.43, -18.52) * mm, "mid": v(-17.4, -23.35) * mm, "end": v(-1.3, -3.56) * mm});
            skArc(sketch, "E19.3.2", {"start": v(-44.92, -11.3) * mm, "mid": v(-21.14, -21.63) * mm, "end": v(-3.86, -2.3) * mm});
            skLineSegment(sketch, "E19.3.3", {"start": v(-1.3, -3.56) * mm, "end": v(-3.86, -2.3) * mm});
            skLineSegment(sketch, "E19.4.0", {"start": v(-5.18, -46.01) * mm, "end": v(-12.67, -44.56) * mm});
            skArc(sketch, "E19.4.1", {"start": v(-5.18, -46.01) * mm, "mid": v(11.52, -26.73) * mm, "end": v(2.44, -2.9) * mm});
            skArc(sketch, "E19.4.2", {"start": v(-12.67, -44.56) * mm, "mid": v(8.16, -29.12) * mm, "end": v(0.07, -4.5) * mm});
            skLineSegment(sketch, "E19.4.3", {"start": v(2.44, -2.9) * mm, "end": v(0.07, -4.5) * mm});
            skLineSegment(sketch, "E19.5.0", {"start": v(37.26, -27.49) * mm, "end": v(32.25, -33.25) * mm});
            skArc(sketch, "E19.5.1", {"start": v(37.26, -27.49) * mm, "mid": v(28.91, -3.39) * mm, "end": v(3.73, 0.66) * mm});
            skArc(sketch, "E19.5.2", {"start": v(32.25, -33.25) * mm, "mid": v(29.3, -7.5) * mm, "end": v(3.93, -2.19) * mm});
            skLineSegment(sketch, "E19.5.3", {"start": v(3.73, 0.66) * mm, "end": v(3.93, -2.19) * mm});
            skPoint(sketch, "E19.center", {"position": v(0, 0) * mm});
            skSolve(sketch);
        }
        {
            var Q0;
            Q0=makeQuery(id+"F7.imprint","IMPRINT",FACE,{"disambiguationData":[TD([[makeQuery(id+"F7.imprint","IMPRINT",EDGE,{"derivedFrom":sQuery(id+"F7.wireOp",EDGE,"E15")}),1.0]])]});
            var Q1;
            Q1=makeQuery(id+"F7.imprint","IMPRINT",FACE,{"disambiguationData":[TD([[makeQuery(id+"F7.imprint","IMPRINT",EDGE,{"derivedFrom":sQuery(id+"F7.wireOp",EDGE,"E19.1.0")}),-1.0]])]});
            var Q2;
            Q2=makeQuery(id+"F7.imprint","IMPRINT",FACE,{"disambiguationData":[TD([[makeQuery(id+"F7.imprint","IMPRINT",EDGE,{"derivedFrom":sQuery(id+"F7.wireOp",EDGE,"E19.2.0")}),-1.0]])]});
            var Q3;
            Q3=makeQuery(id+"F7.imprint","IMPRINT",FACE,{"disambiguationData":[TD([[makeQuery(id+"F7.imprint","IMPRINT",EDGE,{"derivedFrom":sQuery(id+"F7.wireOp",EDGE,"E19.3.0")}),-1.0]])]});
            var Q4;
            Q4=makeQuery(id+"F7.imprint","IMPRINT",FACE,{"disambiguationData":[TD([[makeQuery(id+"F7.imprint","IMPRINT",EDGE,{"derivedFrom":sQuery(id+"F7.wireOp",EDGE,"E19.4.0")}),-1.0]])]});
            var Q5;
            {var subQ2=sQuery(id+"F7.wireOp",EDGE,"E19.5.0");Q5=makeQuery(id+"F7.imprint","IMPRINT",FACE,{"disambiguationData":[TD([[makeQuery(id+"F7.imprint","IMPRINT",EDGE,{"derivedFrom":subQ2}),-1.0]])]});}
            var Q6;
            {var subQ0=sQuery(id+"F7.wireOp",EDGE,"E19.5.1");var subQ1=sQuery(id+"F7.wireOp",EDGE,"E14");var subQ2=makeQuery(id+"F7.imprint","INTERSECT",VERTEX,{"derivedFrom":[subQ1,subQ0]});Q6=makeQuery(id+"F7.imprint","IMPRINT",FACE,{"disambiguationData":[TD([[makeQuery(id+"F7.imprint","IMPRINT",EDGE,{"disambiguationData":[TD([[subQ2,1.0]])],"derivedFrom":subQ1}),1.0]])]});}
            extrude(context, id + "F8", {"entities" : qUnion([Q0, Q1, Q2, Q3, Q4, Q5, Q6]), "oppositeDirection" : true, "depth" : 5 * mm});
        }
    });
